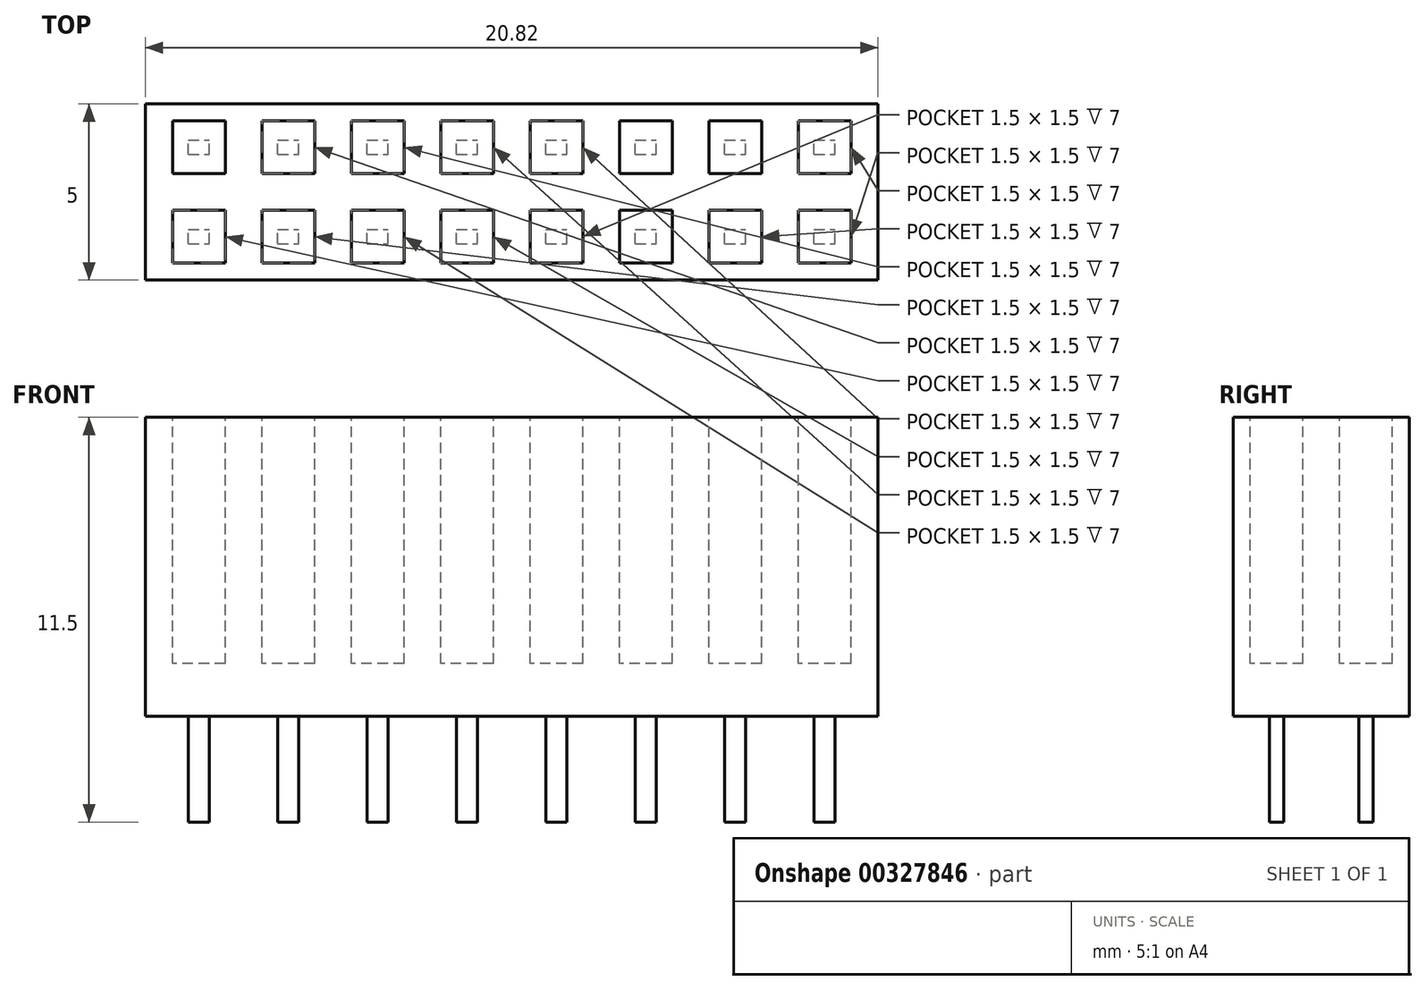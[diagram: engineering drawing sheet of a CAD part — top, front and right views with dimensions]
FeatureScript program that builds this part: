
annotation { "Feature Type Name" : "Feature", "Feature Type Description" : "" }
export const myFeature = defineFeature(function(context is Context, id is Id, definition is map)
    precondition{}
    {
        {
            var Q0;
            Q0=qCreatedBy(makeId("Top.planeOp"),FACE);
            var sketch = newSketch(context, id + "F0", { "sketchPlane" : qUnion([Q0])});
            skLineSegment(sketch, "E0.bottom", {"start": v(-10.4, 2.5) * mm, "end": v(10.4, 2.5) * mm});
            skLineSegment(sketch, "E0.top", {"start": v(-10.4, -2.5) * mm, "end": v(10.4, -2.5) * mm});
            skLineSegment(sketch, "E0.left", {"start": v(-10.4, 2.5) * mm, "end": v(-10.4, -2.5) * mm});
            skLineSegment(sketch, "E0.right", {"start": v(10.4, 2.5) * mm, "end": v(10.4, -2.5) * mm});
            skPoint(sketch, "E0.middle", {"position": v(0, 0) * mm});
            skSolve(sketch);
        }
        {
            var Q0;
            Q0=qSketchRegion(id+"F0",true);
            extrude(context, id + "F1", {"entities" : qUnion([Q0]), "depth" : 8.5 * mm});
        }
        {
            var Q0;
            Q0=makeQuery(id+"F1.opExtrude","CAP_FACE",FACE,{"disambiguationData":[OSD([sQuery(id+"F0.wireOp",EDGE,"E0.bottom"),sQuery(id+"F0.wireOp",EDGE,"E0.top"),sQuery(id+"F0.wireOp",EDGE,"E0.left"),sQuery(id+"F0.wireOp",EDGE,"E0.right")])],"isStart":false});
            var sketch = newSketch(context, id + "F2", { "sketchPlane" : qUnion([Q0])});
            skLineSegment(sketch, "E1.bottom", {"start": v(-8.14, 2.02) * mm, "end": v(-9.64, 2.02) * mm});
            skLineSegment(sketch, "E1.top", {"start": v(-8.14, 0.52) * mm, "end": v(-9.64, 0.52) * mm});
            skLineSegment(sketch, "E1.left", {"start": v(-8.14, 2.02) * mm, "end": v(-8.14, 0.52) * mm});
            skLineSegment(sketch, "E1.right", {"start": v(-9.64, 2.02) * mm, "end": v(-9.64, 0.52) * mm});
            skPoint(sketch, "E1.middle", {"position": v(-8.89, 1.27) * mm});
            skLineSegment(sketch, "E2.0.1.0", {"start": v(-8.14, -0.52) * mm, "end": v(-9.64, -0.52) * mm});
            skLineSegment(sketch, "E2.0.1.1", {"start": v(-8.14, -0.52) * mm, "end": v(-8.14, -2.02) * mm});
            skLineSegment(sketch, "E2.0.1.2", {"start": v(-9.64, -0.52) * mm, "end": v(-9.64, -2.02) * mm});
            skLineSegment(sketch, "E2.0.1.3", {"start": v(-8.14, -2.02) * mm, "end": v(-9.64, -2.02) * mm});
            skLineSegment(sketch, "E2.1.0.0", {"start": v(-5.6, 2.02) * mm, "end": v(-7.1, 2.02) * mm});
            skLineSegment(sketch, "E2.1.0.1", {"start": v(-5.6, 2.02) * mm, "end": v(-5.6, 0.52) * mm});
            skLineSegment(sketch, "E2.1.0.2", {"start": v(-7.1, 2.02) * mm, "end": v(-7.1, 0.52) * mm});
            skLineSegment(sketch, "E2.1.0.3", {"start": v(-5.6, 0.52) * mm, "end": v(-7.1, 0.52) * mm});
            skLineSegment(sketch, "E2.1.1.0", {"start": v(-5.6, -0.52) * mm, "end": v(-7.1, -0.52) * mm});
            skLineSegment(sketch, "E2.1.1.1", {"start": v(-5.6, -0.52) * mm, "end": v(-5.6, -2.02) * mm});
            skLineSegment(sketch, "E2.1.1.2", {"start": v(-7.1, -0.52) * mm, "end": v(-7.1, -2.02) * mm});
            skLineSegment(sketch, "E2.1.1.3", {"start": v(-5.6, -2.02) * mm, "end": v(-7.1, -2.02) * mm});
            skLineSegment(sketch, "E2.2.0.0", {"start": v(-3.06, 2.02) * mm, "end": v(-4.56, 2.02) * mm});
            skLineSegment(sketch, "E2.2.0.1", {"start": v(-3.06, 2.02) * mm, "end": v(-3.06, 0.52) * mm});
            skLineSegment(sketch, "E2.2.0.2", {"start": v(-4.56, 2.02) * mm, "end": v(-4.56, 0.52) * mm});
            skLineSegment(sketch, "E2.2.0.3", {"start": v(-3.06, 0.52) * mm, "end": v(-4.56, 0.52) * mm});
            skLineSegment(sketch, "E2.2.1.0", {"start": v(-3.06, -0.52) * mm, "end": v(-4.56, -0.52) * mm});
            skLineSegment(sketch, "E2.2.1.1", {"start": v(-3.06, -0.52) * mm, "end": v(-3.06, -2.02) * mm});
            skLineSegment(sketch, "E2.2.1.2", {"start": v(-4.56, -0.52) * mm, "end": v(-4.56, -2.02) * mm});
            skLineSegment(sketch, "E2.2.1.3", {"start": v(-3.06, -2.02) * mm, "end": v(-4.56, -2.02) * mm});
            skLineSegment(sketch, "E2.3.0.0", {"start": v(-0.52, 2.02) * mm, "end": v(-2.02, 2.02) * mm});
            skLineSegment(sketch, "E2.3.0.1", {"start": v(-0.52, 2.02) * mm, "end": v(-0.52, 0.52) * mm});
            skLineSegment(sketch, "E2.3.0.2", {"start": v(-2.02, 2.02) * mm, "end": v(-2.02, 0.52) * mm});
            skLineSegment(sketch, "E2.3.0.3", {"start": v(-0.52, 0.52) * mm, "end": v(-2.02, 0.52) * mm});
            skLineSegment(sketch, "E2.3.1.0", {"start": v(-0.52, -0.52) * mm, "end": v(-2.02, -0.52) * mm});
            skLineSegment(sketch, "E2.3.1.1", {"start": v(-0.52, -0.52) * mm, "end": v(-0.52, -2.02) * mm});
            skLineSegment(sketch, "E2.3.1.2", {"start": v(-2.02, -0.52) * mm, "end": v(-2.02, -2.02) * mm});
            skLineSegment(sketch, "E2.3.1.3", {"start": v(-0.52, -2.02) * mm, "end": v(-2.02, -2.02) * mm});
            skLineSegment(sketch, "E2.4.0.0", {"start": v(2.02, 2.02) * mm, "end": v(0.52, 2.02) * mm});
            skLineSegment(sketch, "E2.4.0.1", {"start": v(2.02, 2.02) * mm, "end": v(2.02, 0.52) * mm});
            skLineSegment(sketch, "E2.4.0.2", {"start": v(0.52, 2.02) * mm, "end": v(0.52, 0.52) * mm});
            skLineSegment(sketch, "E2.4.0.3", {"start": v(2.02, 0.52) * mm, "end": v(0.52, 0.52) * mm});
            skLineSegment(sketch, "E2.4.1.0", {"start": v(2.02, -0.52) * mm, "end": v(0.52, -0.52) * mm});
            skLineSegment(sketch, "E2.4.1.1", {"start": v(2.02, -0.52) * mm, "end": v(2.02, -2.02) * mm});
            skLineSegment(sketch, "E2.4.1.2", {"start": v(0.52, -0.52) * mm, "end": v(0.52, -2.02) * mm});
            skLineSegment(sketch, "E2.4.1.3", {"start": v(2.02, -2.02) * mm, "end": v(0.52, -2.02) * mm});
            skLineSegment(sketch, "E2.5.0.0", {"start": v(4.56, 2.02) * mm, "end": v(3.06, 2.02) * mm});
            skLineSegment(sketch, "E2.5.0.1", {"start": v(4.56, 2.02) * mm, "end": v(4.56, 0.52) * mm});
            skLineSegment(sketch, "E2.5.0.2", {"start": v(3.06, 2.02) * mm, "end": v(3.06, 0.52) * mm});
            skLineSegment(sketch, "E2.5.0.3", {"start": v(4.56, 0.52) * mm, "end": v(3.06, 0.52) * mm});
            skLineSegment(sketch, "E2.5.1.0", {"start": v(4.56, -0.52) * mm, "end": v(3.06, -0.52) * mm});
            skLineSegment(sketch, "E2.5.1.1", {"start": v(4.56, -0.52) * mm, "end": v(4.56, -2.02) * mm});
            skLineSegment(sketch, "E2.5.1.2", {"start": v(3.06, -0.52) * mm, "end": v(3.06, -2.02) * mm});
            skLineSegment(sketch, "E2.5.1.3", {"start": v(4.56, -2.02) * mm, "end": v(3.06, -2.02) * mm});
            skLineSegment(sketch, "E2.direction1", {"start": v(-9.64, 2.02) * mm, "end": v(-7.1, 2.02) * mm, "construction": true});
            skLineSegment(sketch, "E2.direction2", {"start": v(-9.64, 2.02) * mm, "end": v(-9.64, -0.52) * mm, "construction": true});
            skLineSegment(sketch, "E3.0.6.0", {"start": v(7.1, 2.02) * mm, "end": v(5.6, 2.02) * mm});
            skLineSegment(sketch, "E3.3.6.0", {"start": v(7.1, 2.02) * mm, "end": v(7.1, 0.52) * mm});
            skLineSegment(sketch, "E3.6.6.0", {"start": v(5.6, 2.02) * mm, "end": v(5.6, 0.52) * mm});
            skLineSegment(sketch, "E3.9.6.0", {"start": v(7.1, 0.52) * mm, "end": v(5.6, 0.52) * mm});
            skLineSegment(sketch, "E3.0.6.1", {"start": v(7.1, -0.52) * mm, "end": v(5.6, -0.52) * mm});
            skLineSegment(sketch, "E3.3.6.1", {"start": v(7.1, -0.52) * mm, "end": v(7.1, -2.02) * mm});
            skLineSegment(sketch, "E3.6.6.1", {"start": v(5.6, -0.52) * mm, "end": v(5.6, -2.02) * mm});
            skLineSegment(sketch, "E3.9.6.1", {"start": v(7.1, -2.02) * mm, "end": v(5.6, -2.02) * mm});
            skLineSegment(sketch, "E3.0.7.0", {"start": v(9.64, 2.02) * mm, "end": v(8.14, 2.02) * mm});
            skLineSegment(sketch, "E3.3.7.0", {"start": v(9.64, 2.02) * mm, "end": v(9.64, 0.52) * mm});
            skLineSegment(sketch, "E3.6.7.0", {"start": v(8.14, 2.02) * mm, "end": v(8.14, 0.52) * mm});
            skLineSegment(sketch, "E3.9.7.0", {"start": v(9.64, 0.52) * mm, "end": v(8.14, 0.52) * mm});
            skLineSegment(sketch, "E3.0.7.1", {"start": v(9.64, -0.52) * mm, "end": v(8.14, -0.52) * mm});
            skLineSegment(sketch, "E3.3.7.1", {"start": v(9.64, -0.52) * mm, "end": v(9.64, -2.02) * mm});
            skLineSegment(sketch, "E3.6.7.1", {"start": v(8.14, -0.52) * mm, "end": v(8.14, -2.02) * mm});
            skLineSegment(sketch, "E3.9.7.1", {"start": v(9.64, -2.02) * mm, "end": v(8.14, -2.02) * mm});
            skSolve(sketch);
        }
        {
            var Q0;
            Q0=qSketchRegion(id+"F2",true);
            extrude(context, id + "F3", {"entities" : qUnion([Q0]), "operationType" : NewBodyOperationType.REMOVE, "oppositeDirection" : true, "depth" : 7 * mm});
        }
        {
            var Q0;
            Q0=makeQuery(id+"F1.opExtrude","CAP_FACE",FACE,{"disambiguationData":[OSD([sQuery(id+"F0.wireOp",EDGE,"E0.bottom"),sQuery(id+"F0.wireOp",EDGE,"E0.top"),sQuery(id+"F0.wireOp",EDGE,"E0.left"),sQuery(id+"F0.wireOp",EDGE,"E0.right")])],"isStart":true});
            var sketch = newSketch(context, id + "F4", { "sketchPlane" : qUnion([Q0])});
            skLineSegment(sketch, "E4.bottom", {"start": v(-9.19, 1.47) * mm, "end": v(-8.59, 1.47) * mm});
            skLineSegment(sketch, "E4.top", {"start": v(-9.19, 1.07) * mm, "end": v(-8.59, 1.07) * mm});
            skLineSegment(sketch, "E4.left", {"start": v(-9.19, 1.47) * mm, "end": v(-9.19, 1.07) * mm});
            skLineSegment(sketch, "E4.right", {"start": v(-8.59, 1.47) * mm, "end": v(-8.59, 1.07) * mm});
            skPoint(sketch, "E4.middle", {"position": v(-8.89, 1.27) * mm});
            skPoint(sketch, "E5.0", {"position": v(-9.64, 2.02) * mm});
            skPoint(sketch, "E5.1", {"position": v(-8.14, 0.52) * mm});
            skLineSegment(sketch, "E6", {"start": v(-9.64, 2.02) * mm, "end": v(-8.14, 0.52) * mm, "construction": true});
            skLineSegment(sketch, "E7.0.1.0", {"start": v(-9.19, -1.07) * mm, "end": v(-8.59, -1.07) * mm});
            skLineSegment(sketch, "E7.0.1.1", {"start": v(-9.19, -1.07) * mm, "end": v(-9.19, -1.47) * mm});
            skLineSegment(sketch, "E7.0.1.2", {"start": v(-9.19, -1.47) * mm, "end": v(-8.59, -1.47) * mm});
            skLineSegment(sketch, "E7.0.1.3", {"start": v(-8.59, -1.07) * mm, "end": v(-8.59, -1.47) * mm});
            skLineSegment(sketch, "E7.1.0.0", {"start": v(-6.65, 1.47) * mm, "end": v(-6.05, 1.47) * mm});
            skLineSegment(sketch, "E7.1.0.1", {"start": v(-6.65, 1.47) * mm, "end": v(-6.65, 1.07) * mm});
            skLineSegment(sketch, "E7.1.0.2", {"start": v(-6.65, 1.07) * mm, "end": v(-6.05, 1.07) * mm});
            skLineSegment(sketch, "E7.1.0.3", {"start": v(-6.05, 1.47) * mm, "end": v(-6.05, 1.07) * mm});
            skLineSegment(sketch, "E7.1.1.0", {"start": v(-6.65, -1.07) * mm, "end": v(-6.05, -1.07) * mm});
            skLineSegment(sketch, "E7.1.1.1", {"start": v(-6.65, -1.07) * mm, "end": v(-6.65, -1.47) * mm});
            skLineSegment(sketch, "E7.1.1.2", {"start": v(-6.65, -1.47) * mm, "end": v(-6.05, -1.47) * mm});
            skLineSegment(sketch, "E7.1.1.3", {"start": v(-6.05, -1.07) * mm, "end": v(-6.05, -1.47) * mm});
            skLineSegment(sketch, "E7.2.0.0", {"start": v(-4.1, 1.47) * mm, "end": v(-3.5, 1.47) * mm});
            skLineSegment(sketch, "E7.2.0.1", {"start": v(-4.1, 1.47) * mm, "end": v(-4.1, 1.07) * mm});
            skLineSegment(sketch, "E7.2.0.2", {"start": v(-4.1, 1.07) * mm, "end": v(-3.5, 1.07) * mm});
            skLineSegment(sketch, "E7.2.0.3", {"start": v(-3.5, 1.47) * mm, "end": v(-3.5, 1.07) * mm});
            skLineSegment(sketch, "E7.2.1.0", {"start": v(-4.1, -1.07) * mm, "end": v(-3.5, -1.07) * mm});
            skLineSegment(sketch, "E7.2.1.1", {"start": v(-4.1, -1.07) * mm, "end": v(-4.1, -1.47) * mm});
            skLineSegment(sketch, "E7.2.1.2", {"start": v(-4.1, -1.47) * mm, "end": v(-3.5, -1.47) * mm});
            skLineSegment(sketch, "E7.2.1.3", {"start": v(-3.5, -1.07) * mm, "end": v(-3.5, -1.47) * mm});
            skLineSegment(sketch, "E7.3.0.0", {"start": v(-1.57, 1.47) * mm, "end": v(-0.97, 1.47) * mm});
            skLineSegment(sketch, "E7.3.0.1", {"start": v(-1.57, 1.47) * mm, "end": v(-1.57, 1.07) * mm});
            skLineSegment(sketch, "E7.3.0.2", {"start": v(-1.57, 1.07) * mm, "end": v(-0.97, 1.07) * mm});
            skLineSegment(sketch, "E7.3.0.3", {"start": v(-0.97, 1.47) * mm, "end": v(-0.97, 1.07) * mm});
            skLineSegment(sketch, "E7.3.1.0", {"start": v(-1.57, -1.07) * mm, "end": v(-0.97, -1.07) * mm});
            skLineSegment(sketch, "E7.3.1.1", {"start": v(-1.57, -1.07) * mm, "end": v(-1.57, -1.47) * mm});
            skLineSegment(sketch, "E7.3.1.2", {"start": v(-1.57, -1.47) * mm, "end": v(-0.97, -1.47) * mm});
            skLineSegment(sketch, "E7.3.1.3", {"start": v(-0.97, -1.07) * mm, "end": v(-0.97, -1.47) * mm});
            skLineSegment(sketch, "E7.4.0.0", {"start": v(0.97, 1.47) * mm, "end": v(1.57, 1.47) * mm});
            skLineSegment(sketch, "E7.4.0.1", {"start": v(0.97, 1.47) * mm, "end": v(0.97, 1.07) * mm});
            skLineSegment(sketch, "E7.4.0.2", {"start": v(0.97, 1.07) * mm, "end": v(1.57, 1.07) * mm});
            skLineSegment(sketch, "E7.4.0.3", {"start": v(1.57, 1.47) * mm, "end": v(1.57, 1.07) * mm});
            skLineSegment(sketch, "E7.4.1.0", {"start": v(0.97, -1.07) * mm, "end": v(1.57, -1.07) * mm});
            skLineSegment(sketch, "E7.4.1.1", {"start": v(0.97, -1.07) * mm, "end": v(0.97, -1.47) * mm});
            skLineSegment(sketch, "E7.4.1.2", {"start": v(0.97, -1.47) * mm, "end": v(1.57, -1.47) * mm});
            skLineSegment(sketch, "E7.4.1.3", {"start": v(1.57, -1.07) * mm, "end": v(1.57, -1.47) * mm});
            skLineSegment(sketch, "E7.5.0.0", {"start": v(3.51, 1.47) * mm, "end": v(4.11, 1.47) * mm});
            skLineSegment(sketch, "E7.5.0.1", {"start": v(3.51, 1.47) * mm, "end": v(3.51, 1.07) * mm});
            skLineSegment(sketch, "E7.5.0.2", {"start": v(3.51, 1.07) * mm, "end": v(4.11, 1.07) * mm});
            skLineSegment(sketch, "E7.5.0.3", {"start": v(4.11, 1.47) * mm, "end": v(4.11, 1.07) * mm});
            skLineSegment(sketch, "E7.5.1.0", {"start": v(3.51, -1.07) * mm, "end": v(4.11, -1.07) * mm});
            skLineSegment(sketch, "E7.5.1.1", {"start": v(3.51, -1.07) * mm, "end": v(3.51, -1.47) * mm});
            skLineSegment(sketch, "E7.5.1.2", {"start": v(3.51, -1.47) * mm, "end": v(4.11, -1.47) * mm});
            skLineSegment(sketch, "E7.5.1.3", {"start": v(4.11, -1.07) * mm, "end": v(4.11, -1.47) * mm});
            skLineSegment(sketch, "E7.direction1", {"start": v(-9.19, 1.47) * mm, "end": v(-6.65, 1.47) * mm, "construction": true});
            skLineSegment(sketch, "E7.direction2", {"start": v(-9.19, 1.47) * mm, "end": v(-9.19, -1.07) * mm, "construction": true});
            skLineSegment(sketch, "E8.0.6.0", {"start": v(6.05, 1.47) * mm, "end": v(6.65, 1.47) * mm});
            skLineSegment(sketch, "E8.3.6.0", {"start": v(6.05, 1.47) * mm, "end": v(6.05, 1.07) * mm});
            skLineSegment(sketch, "E8.6.6.0", {"start": v(6.05, 1.07) * mm, "end": v(6.65, 1.07) * mm});
            skLineSegment(sketch, "E8.9.6.0", {"start": v(6.65, 1.47) * mm, "end": v(6.65, 1.07) * mm});
            skLineSegment(sketch, "E8.0.6.1", {"start": v(6.05, -1.07) * mm, "end": v(6.65, -1.07) * mm});
            skLineSegment(sketch, "E8.3.6.1", {"start": v(6.05, -1.07) * mm, "end": v(6.05, -1.47) * mm});
            skLineSegment(sketch, "E8.6.6.1", {"start": v(6.05, -1.47) * mm, "end": v(6.65, -1.47) * mm});
            skLineSegment(sketch, "E8.9.6.1", {"start": v(6.65, -1.07) * mm, "end": v(6.65, -1.47) * mm});
            skLineSegment(sketch, "E8.0.7.0", {"start": v(8.6, 1.47) * mm, "end": v(9.2, 1.47) * mm});
            skLineSegment(sketch, "E8.3.7.0", {"start": v(8.6, 1.47) * mm, "end": v(8.6, 1.07) * mm});
            skLineSegment(sketch, "E8.6.7.0", {"start": v(8.6, 1.07) * mm, "end": v(9.2, 1.07) * mm});
            skLineSegment(sketch, "E8.9.7.0", {"start": v(9.2, 1.47) * mm, "end": v(9.2, 1.07) * mm});
            skLineSegment(sketch, "E8.0.7.1", {"start": v(8.6, -1.07) * mm, "end": v(9.2, -1.07) * mm});
            skLineSegment(sketch, "E8.3.7.1", {"start": v(8.6, -1.07) * mm, "end": v(8.6, -1.47) * mm});
            skLineSegment(sketch, "E8.6.7.1", {"start": v(8.6, -1.47) * mm, "end": v(9.2, -1.47) * mm});
            skLineSegment(sketch, "E8.9.7.1", {"start": v(9.2, -1.07) * mm, "end": v(9.2, -1.47) * mm});
            skSolve(sketch);
        }
        {
            var Q0;
            Q0=qSketchRegion(id+"F4",true);
            extrude(context, id + "F5", {"entities" : qUnion([Q0]), "depth" : 3 * mm});
        }
    });
